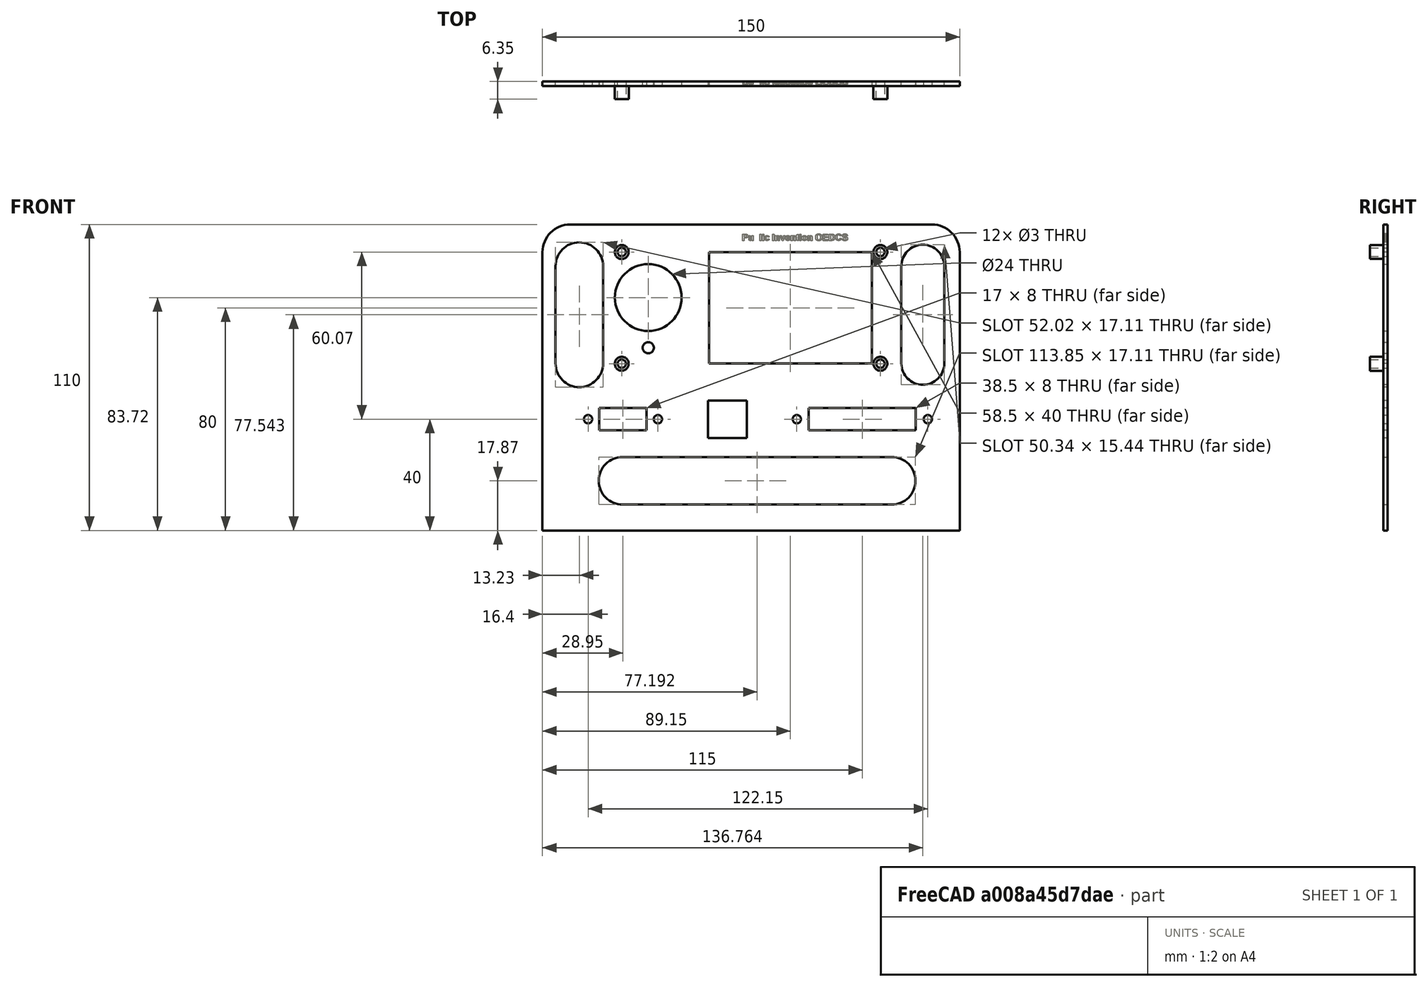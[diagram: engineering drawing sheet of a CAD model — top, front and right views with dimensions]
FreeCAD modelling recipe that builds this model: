
FCSTD DOCUMENT  (FreeCAD 0.19R24291 (Git))
Label: MountMini12864
License: All rights reserved
LicenseURL: http://en.wikipedia.org/wiki/All_rights_reserved
objects: TechDraw::DrawViewDimension×19, Sketcher::SketchObject×5, PartDesign::Pocket×4, PartDesign::Pad×2, Spreadsheet::Sheet×1, TechDraw::DrawSVGTemplate×1, PartDesign::Fillet×1, Part::Part2DObjectPython×1, PartDesign::Body×1, App::Part×1, TechDraw::DrawViewPart×1, TechDraw::DrawPage×1
note: 21 computed .brp shape members not serialized (recipe doc carries the construction recipe); baked Part::Feature solids carry a one-line shape summary decoded from their .brp

FEATURE [Sketcher::SketchObject] Sketch
  FullyConstrained = true
  MapMode = 5
  Placement = pos=(0,0,0) rot=(1,0,0;1.5708rad)
  Support = -> [XZ_Plane001]
  expr: Constraints[10] = <<Spreadsheet>>.Height
  expr: Constraints[9] = <<Spreadsheet>>.Width
  expr: Constraints[11] = <<Spreadsheet>>.OffsetVert
  expr: Constraints[12] = <<Spreadsheet>>.OffsetHorz
  sketch-geometry (5):
    g0: LineSegment StartX=-55 StartY=45 StartZ=0 EndX=95 EndY=45 EndZ=0
    g1: LineSegment StartX=95 StartY=45 StartZ=0 EndX=95 EndY=-65 EndZ=0
    g2: LineSegment StartX=95 StartY=-65 StartZ=0 EndX=-55 EndY=-65 EndZ=0
    g3: LineSegment StartX=-55 StartY=-65 StartZ=0 EndX=-55 EndY=45 EndZ=0
    g4: GeomPoint X=20 Y=-10 Z=0
  constraints (13):
    c: Coincident(g0,g1)
    c: Coincident(g1,g2)
    c: Coincident(g2,g3)
    c: Coincident(g3,g0)
    c: Horizontal(g0)
    c: Horizontal(g2)
    c: Vertical(g1)
    c: Vertical(g3)
    c: Symmetric(g0,g1,g4)
    c: DistanceX(g0,g0) = 150
    c: DistanceY(g3,g3) = 110
    c: DistanceY(g4,g-1) = 10
    c: DistanceX(g-1,g4) = 20
FEATURE [PartDesign::Pad] Pad  label="Pad Body"
  Direction = (1,1,1)
  Length = 1.5875
  Length2 = 100
  Placement = pos=(0,0,0) rot=(1,0,0;1.5708rad)
  Profile = -> Sketch
  Type = 0
  expr: Length = <<Spreadsheet>>.Thickness
FEATURE [Spreadsheet::Sheet] Spreadsheet
  cells = A1=MountMini12864; A2=Place a center point. Locate that point at Horz and Vertical Offset; A3=Place a rectangle around the point. ; A4=Select upper left corner, lower right cornder and center point. Set symetery; A5=Set Width to Width parameter (below), Set Height to Height Parameter below.; A6=Close the now fully parameterized and constrinaed sketch.; A7=Pad the sketch to the Depth prameter (below).; A9=Body; A10=OffsetHorz; B10(OffsetHorz)==20mm; A11=OffsetVert; B11(OffsetVert)==10mm; A13=Width; B13(Width)==150mm; C13=PCB is 189mm; A14=Height; B14(Height)==110mm; A15=Depth; B15(Depth)==3mm; A16=Thickness; B16(Thickness)==C16; C16==25.4 / 16; A18=DisplayMount; A19=OffsetMountHorz; B19(OffsetMountHorz)==20mm; C19=Toward left; A20=OffsetMountVert; B20(OffsetMountVert)==15mm; C21=From drawing; A22=DisplayMountWidth; B22(DisplayMountWidth)==C22; C22==101.99 - 8.99; A23=DisplayMountHeight; B23(DisplayMountHeight)==C23; C23==44 - 3.86; A24=DisplayMountHoleDiameter; B24(DisplayMountHoleDiameter)==3mm; A25=DisplayMountStandOffLength; B25(DisplayMountStandOffLength)==C25 * 25.4; C25=0.25; A27=OffsetDisplayHorz; B27(OffsetDisplayHorz)==61.6mm; C27=From edge; D27==70.59 - 8.99; A28=OffsetDisplayVert; B28(OffsetDisplayVert)==15mm; C28=From drawing; A29=DisplayWidth; B29(DisplayWidth)==58.5mm; C29==70.59 - 12.39; A30=DisplayHeight; B30(DisplayHeight)==40mm; C30==38.8mm; A32=OffsetEncoderHorz; B32(OffsetEncoderHorz)==12.53 - 3; C32=Guess; A33=OffserEncoderVert; B33(OffserEncoderVert)==(32.71 + 20.87) / 2 - 3; C33=Up from Mount; A34=EncoderDiameter; B34(EncoderDiameter)==24mm; C34=Measured Knob; A36=OffsetResetHorz; B36(OffsetResetHorz)==B32; C36=same as encoder; A37=OffserResetVert; B37(OffserResetVert)==5.75mm; C37=Up from Mount; A38=ResetDiameter; B38(ResetDiameter)==4mm; A41=DB25 Mount; A42=OffsetDB25MountHorz; B42(OffsetDB25MountHorz)==60mm; C42=This moves DB25, RJ12, and DB9; A43=OffsetDB25MountVert; B43(OffsetDB25MountVert)==25mm; C43=Down from center; A45=DB25MountWidth; B45(DB25MountWidth)==38.5mm; A46=DB25MountHeight; B46(DB25MountHeight)==8mm; A47=DB25MountHoleSpace; B47(DB25MountHoleSpace)==47.1mm; A48=DB25MountHoleDiameter; B48(DB25MountHoleDiameter)==3mm; A51=RJ12 Connector; A52=OffsetRJ12MountHorz; B52(OffsetRJ12MountHorz)==48.5mm; C52=From DB25; A53=OffsetRJ12MountVert; B53(OffsetRJ12MountVert)==25mm; A55=RJ12Width; B55(RJ12Width)==14mm; C55=13.5 mm measured; A56=RJ12Height; B56(RJ12Height)==13.5mm; C56=12.5 mm measured; A59=DB9 Mount; A60=OffsetDB9MountHorz; B60(OffsetDB9MountHorz)==86.05mm; A61=OffsetDB9MountVert; B61(OffsetDB9MountVert)==25mm; C61=Down from center; A63=DB9MountWidth; B63(DB9MountWidth)=17; C63==16.3mm; A64=DB9MountHeight; B64(DB9MountHeight)==8mm; A65=DB9MountHoleSpace; B65(DB9MountHoleSpace)==25.1mm; A66=DB9MountHoleDiameter; B66(DB9MountHoleDiameter)==3mm
FEATURE [Sketcher::SketchObject] Sketch001
  FullyConstrained = true
  MapMode = 5
  Placement = pos=(0,0,0) rot=(-1,0,0;1.5708rad)
  Support = -> [Pad]
  expr: Constraints[39] = <<Spreadsheet>>.OffsetMountHorz
  expr: Constraints[38] = <<Spreadsheet>>.OffsetEncoderHorz
  expr: Constraints[29] = <<Spreadsheet>>.DisplayWidth
  expr: Constraints[32] = <<Spreadsheet>>.OffsetDisplayHorz
  expr: Constraints[37] = <<Spreadsheet>>.OffserEncoderVert
  expr: Constraints[36] = <<Spreadsheet>>.OffserResetVert
  expr: Constraints[34] = <<Spreadsheet>>.ResetDiameter
  expr: Constraints[18] = <<Spreadsheet>>.DisplayMountHeight
  expr: Constraints[30] = <<Spreadsheet>>.DisplayHeight
  expr: Constraints[19] = <<Spreadsheet>>.OffsetMountVert
  expr: Constraints[33] = <<Spreadsheet>>.EncoderDiameter
  expr: Constraints[17] = <<Spreadsheet>>.DisplayMountWidth
  expr: Constraints[12] = <<Spreadsheet>>.DisplayMountHoleDiameter
  sketch-geometry (16):
    g0: LineSegment StartX=-26.5 StartY=5.07 StartZ=0 EndX=66.5 EndY=5.07 EndZ=0
    g1: LineSegment StartX=66.5 StartY=5.07 StartZ=0 EndX=66.5 EndY=-35.07 EndZ=0
    g2: LineSegment StartX=66.5 StartY=-35.07 StartZ=0 EndX=-26.5 EndY=-35.07 EndZ=0
    g3: LineSegment StartX=-26.5 StartY=-35.07 StartZ=0 EndX=-26.5 EndY=5.07 EndZ=0
    g4: GeomPoint X=20 Y=-15 Z=0
    g5: Circle CenterX=-26.5 CenterY=5.07 CenterZ=0 NormalX=0 NormalY=0 NormalZ=1 AngleXU=0 Radius=1.5
    g6: Circle CenterX=-26.5 CenterY=-35.07 CenterZ=0 NormalX=0 NormalY=0 NormalZ=1 AngleXU=0 Radius=1.5
    g7: Circle CenterX=66.5 CenterY=-35.07 CenterZ=0 NormalX=0 NormalY=0 NormalZ=1 AngleXU=0 Radius=1.5
    g8: Circle CenterX=66.5 CenterY=5.07 CenterZ=0 NormalX=0 NormalY=0 NormalZ=1 AngleXU=0 Radius=1.5
    g9: LineSegment StartX=4.9 StartY=5 StartZ=0 EndX=63.4 EndY=5 EndZ=0
    g10: LineSegment StartX=63.4 StartY=5 StartZ=0 EndX=63.4 EndY=-35 EndZ=0
    g11: LineSegment StartX=63.4 StartY=-35 StartZ=0 EndX=4.9 EndY=-35 EndZ=0
    g12: LineSegment StartX=4.9 StartY=-35 StartZ=0 EndX=4.9 EndY=5 EndZ=0
    g13: GeomPoint X=34.15 Y=-15 Z=0
    g14: Circle CenterX=-16.97 CenterY=-18.72 CenterZ=0 NormalX=0 NormalY=0 NormalZ=1 AngleXU=0 Radius=12
    g15: Circle CenterX=-16.97 CenterY=-0.68 CenterZ=0 NormalX=0 NormalY=0 NormalZ=1 AngleXU=0 Radius=2
  constraints (40):
    c: Coincident(g0,g1)
    c: Coincident(g1,g2)
    c: Coincident(g2,g3)
    c: Coincident(g3,g0)
    c: Horizontal(g0)
    c: Horizontal(g2)
    c: Vertical(g1)
    c: Vertical(g3)
    c: Symmetric(g0,g1,g4)
    c: Equal(g8,g7)
    c: Equal(g7,g6)
    c: Equal(g6,g5)
    c: Diameter(g5) = 3
    c: Coincident(g5,g0)
    c: Coincident(g6,g2)
    c: Coincident(g7,g1)
    c: Coincident(g8,g0)
    c: DistanceX(g0,g0) = 93
    c: DistanceY(g3,g3) = 40.14
    c: DistanceY(g4,g-1) = 15
    c: Coincident(g9,g10)
    c: Coincident(g10,g11)
    c: Coincident(g11,g12)
    c: Coincident(g12,g9)
    c: Horizontal(g9)
    c: Horizontal(g11)
    c: Vertical(g10)
    c: Vertical(g12)
    c: Symmetric(g9,g10,g13)
    c: DistanceX(g9,g9) = 58.5
    c: DistanceY(g10,g10) = 40
    c: Horizontal(g13,g4)
    c: DistanceX(g9,g8) = 61.6
    c: Diameter(g14) = 24
    c: Diameter(g15) = 4
    c: Vertical(g14,g15)
    c: DistanceY(g15,g5) = 5.75
    c: DistanceY(g14,g5) = 23.79
    c: DistanceX(g5,g14) = 9.53
    c: DistanceX(g-1,g4) = 20
FEATURE [PartDesign::Pocket] Pocket  label="PocketDisplayMountHoles"
  BaseFeature = -> Pad
  Length = 5
  Length2 = 100
  Placement = pos=(0,0,0) rot=(1,0,0;1.5708rad)
  Profile = -> Sketch001
  Type = 1
FEATURE [Sketcher::SketchObject] Sketch002
  FullyConstrained = true
  MapMode = 5
  Placement = pos=(0,0,0) rot=(-1,0,0;1.5708rad)
  Support = -> [Pocket]
  expr: Constraints[48] = <<Spreadsheet>>.DB9MountHoleSpace
  expr: Constraints[45] = <<Spreadsheet>>.OffsetDB9MountHorz
  expr: Constraints[42] = <<Spreadsheet>>.DB9MountWidth
  expr: Constraints[30] = <<Spreadsheet>>.RJ12Height
  expr: Constraints[32] = <<Spreadsheet>>.OffsetRJ12MountHorz
  expr: Constraints[29] = <<Spreadsheet>>.RJ12Width
  expr: Constraints[19] = <<Spreadsheet>>.OffsetDB25MountHorz
  expr: Constraints[43] = <<Spreadsheet>>.DB9MountHeight
  expr: Constraints[18] = <<Spreadsheet>>.DB25MountHoleSpace
  expr: Constraints[14] = <<Spreadsheet>>.DB25MountHoleDiameter
  expr: Constraints[9] = <<Spreadsheet>>.DB25MountWidth
  expr: Constraints[11] = <<Spreadsheet>>.OffsetDB25MountVert
  expr: Constraints[10] = <<Spreadsheet>>.DB25MountHeight
  sketch-geometry (21):
    g0: LineSegment StartX=40.75 StartY=29 StartZ=0 EndX=79.25 EndY=29 EndZ=0
    g1: LineSegment StartX=79.25 StartY=29 StartZ=0 EndX=79.25 EndY=21 EndZ=0
    g2: LineSegment StartX=79.25 StartY=21 StartZ=0 EndX=40.75 EndY=21 EndZ=0
    g3: LineSegment StartX=40.75 StartY=21 StartZ=0 EndX=40.75 EndY=29 EndZ=0
    g4: GeomPoint X=60 Y=25 Z=0
    g5: LineSegment StartX=36.45 StartY=25 StartZ=0 EndX=83.55 EndY=25 EndZ=0
    g6: Circle CenterX=36.45 CenterY=25 CenterZ=0 NormalX=0 NormalY=0 NormalZ=1 AngleXU=0 Radius=1.5
    g7: Circle CenterX=83.55 CenterY=25 CenterZ=0 NormalX=0 NormalY=0 NormalZ=1 AngleXU=0 Radius=1.5
    g8: LineSegment StartX=4.5 StartY=31.75 StartZ=0 EndX=18.5 EndY=31.75 EndZ=0
    g9: LineSegment StartX=18.5 StartY=31.75 StartZ=0 EndX=18.5 EndY=18.25 EndZ=0
    g10: LineSegment StartX=18.5 StartY=18.25 StartZ=0 EndX=4.5 EndY=18.25 EndZ=0
    g11: LineSegment StartX=4.5 StartY=18.25 StartZ=0 EndX=4.5 EndY=31.75 EndZ=0
    g12: GeomPoint X=11.5 Y=25 Z=0
    g13: LineSegment StartX=-34.55 StartY=29 StartZ=0 EndX=-17.55 EndY=29 EndZ=0
    g14: LineSegment StartX=-17.55 StartY=29 StartZ=0 EndX=-17.55 EndY=21 EndZ=0
    g15: LineSegment StartX=-17.55 StartY=21 StartZ=0 EndX=-34.55 EndY=21 EndZ=0
    g16: LineSegment StartX=-34.55 StartY=21 StartZ=0 EndX=-34.55 EndY=29 EndZ=0
    g17: GeomPoint X=-26.05 Y=25 Z=0
    g18: LineSegment StartX=-38.6 StartY=25 StartZ=0 EndX=-13.5 EndY=25 EndZ=0
    g19: Circle CenterX=-38.6 CenterY=25 CenterZ=0 NormalX=0 NormalY=0 NormalZ=1 AngleXU=0 Radius=1.5
    g20: Circle CenterX=-13.5 CenterY=25 CenterZ=0 NormalX=0 NormalY=0 NormalZ=1 AngleXU=0 Radius=1.5
  constraints (53):
    c: Coincident(g0,g1)
    c: Coincident(g1,g2)
    c: Coincident(g2,g3)
    c: Coincident(g3,g0)
    c: Horizontal(g0)
    c: Horizontal(g2)
    c: Vertical(g1)
    c: Vertical(g3)
    c: Symmetric(g0,g1,g4)
    c: DistanceX(g0,g0) = 38.5
    c: DistanceY(g3,g3) = 8
    c: DistanceY(g-1,g4) = 25
    c: Horizontal(g5)
    c: Symmetric(g5,g5,g4)
    c: Diameter(g6) = 3
    c: Equal(g6,g7)
    c: Coincident(g7,g5)
    c: Coincident(g6,g5)
    c: DistanceX(g5,g5) = 47.1
    c: DistanceX(g-1,g4) = 60
    c: Coincident(g8,g9)
    c: Coincident(g9,g10)
    c: Coincident(g10,g11)
    c: Coincident(g11,g8)
    c: Horizontal(g8)
    c: Horizontal(g10)
    c: Vertical(g9)
    c: Vertical(g11)
    c: Symmetric(g8,g9,g12)
    c: DistanceX(g8,g8) = 14
    c: DistanceY(g11,g11) = 13.5
    c: Horizontal(g12,g4)
    c: DistanceX(g12,g4) = 48.5
    c: Coincident(g13,g14)
    c: Coincident(g14,g15)
    c: Coincident(g15,g16)
    c: Coincident(g16,g13)
    c: Horizontal(g13)
    c: Horizontal(g15)
    c: Vertical(g14)
    c: Vertical(g16)
    c: Symmetric(g13,g14,g17)
    c: DistanceX(g13,g13) = 17
    c: DistanceY(g14,g14) = 8
    c: Horizontal(g17,g4)
    c: DistanceX(g17,g4) = 86.05
    c: Horizontal(g18)
    c: Symmetric(g18,g18,g17)
    c: DistanceX(g18,g18) = 25.1
    c: Equal(g19,g20)
    c: Equal(g20,g6)
    c: Coincident(g20,g18)
    c: Coincident(g19,g18)
FEATURE [PartDesign::Pocket] Pocket001  label="PockeDB25Mount"
  BaseFeature = -> Pocket
  Length = 5
  Length2 = 100
  Placement = pos=(0,0,0) rot=(1,0,0;1.5708rad)
  Profile = -> Sketch002
  Type = 1
FEATURE [TechDraw::DrawSVGTemplate] Template
  EditableTexts = Approved1=Approved 1; Approved2=Approved 2; CheckedBy=Checked By; Code=Code; CompanyAddress=1234 Main St; CompanyName=Company Name; DrawingNumber=Drawing Number; DrawingTitle1=Drawing Title 1; DrawingTitle2=Drawing Title 2; DrawingTitle3=Drawing Title 3; DrawnBy=Drawn By; Revision=Rev; Scale=Scale; Sheet=Sheet n of m
  Height = 215.9
  Orientation = 1
  Width = 279.4
FEATURE [Sketcher::SketchObject] Sketch003
  FullyConstrained = true
  MapMode = 5
  Placement = pos=(0,0,0) rot=(-1,0,0;1.5708rad)
  Support = -> [Pocket001]
  expr: Constraints[21] = <<Spreadsheet>>.DisplayMountHoleDiameter
  expr: Constraints[20] = <<Spreadsheet>>.OffsetDisplayVert
  expr: Constraints[19] = <<Spreadsheet>>.OffsetMountHorz
  expr: Constraints[18] = <<Spreadsheet>>.DisplayMountHeight
  expr: Constraints[17] = <<Spreadsheet>>.DisplayMountWidth
  sketch-geometry (13):
    g0: Circle CenterX=-26.5 CenterY=5.07 CenterZ=0 NormalX=0 NormalY=0 NormalZ=1 AngleXU=0 Radius=2.5
    g1: Circle CenterX=-26.5 CenterY=-35.07 CenterZ=0 NormalX=0 NormalY=0 NormalZ=1 AngleXU=0 Radius=2.5
    g2: Circle CenterX=66.5 CenterY=5.07 CenterZ=0 NormalX=0 NormalY=0 NormalZ=1 AngleXU=0 Radius=2.5
    g3: Circle CenterX=66.5 CenterY=-35.07 CenterZ=0 NormalX=0 NormalY=0 NormalZ=1 AngleXU=0 Radius=2.5
    g4: GeomPoint X=20 Y=-15 Z=0
    g5: LineSegment StartX=-26.5 StartY=5.07 StartZ=0 EndX=66.5 EndY=5.07 EndZ=0
    g6: LineSegment StartX=66.5 StartY=5.07 StartZ=0 EndX=66.5 EndY=-35.07 EndZ=0
    g7: LineSegment StartX=66.5 StartY=-35.07 StartZ=0 EndX=-26.5 EndY=-35.07 EndZ=0
    g8: LineSegment StartX=-26.5 StartY=-35.07 StartZ=0 EndX=-26.5 EndY=5.07 EndZ=0
    g9: Circle CenterX=-26.5 CenterY=5.07 CenterZ=0 NormalX=0 NormalY=0 NormalZ=1 AngleXU=0 Radius=1.5
    g10: Circle CenterX=-26.5 CenterY=-35.07 CenterZ=0 NormalX=0 NormalY=0 NormalZ=1 AngleXU=0 Radius=1.5
    g11: Circle CenterX=66.5 CenterY=5.07 CenterZ=0 NormalX=0 NormalY=0 NormalZ=1 AngleXU=0 Radius=1.5
    g12: Circle CenterX=66.5 CenterY=-35.07 CenterZ=0 NormalX=0 NormalY=0 NormalZ=1 AngleXU=0 Radius=1.5
  constraints (29):
    c: Diameter(g0) = 5
    c: Equal(g0,g2)
    c: Equal(g2,g1)
    c: Equal(g1,g3)
    c: Coincident(g5,g6)
    c: Coincident(g6,g7)
    c: Coincident(g7,g8)
    c: Coincident(g8,g5)
    c: Horizontal(g5)
    c: Horizontal(g7)
    c: Vertical(g6)
    c: Vertical(g8)
    c: Symmetric(g5,g6,g4)
    c: Coincident(g0,g5)
    c: Coincident(g1,g7)
    c: Coincident(g3,g6)
    c: Coincident(g2,g5)
    c: DistanceX(g5,g5) = 93
    c: DistanceY(g6,g6) = 40.14
    c: DistanceX(g-1,g4) = 20
    c: DistanceY(g4,g-1) = 15
    c: Diameter(g9) = 3
    c: Equal(g9,g10)
    c: Equal(g10,g12)
    c: Equal(g12,g11)
    c: Coincident(g9,g0)
    c: Coincident(g10,g1)
    c: Coincident(g3,g12)
    c: Coincident(g2,g11)
FEATURE [PartDesign::Pad] Pad001  label="Pad001MountStandoff"
  BaseFeature = -> Pocket001
  Direction = (1,1,1)
  Length = 6.35
  Length2 = 100
  Placement = pos=(0,0,0) rot=(1,0,0;1.5708rad)
  Profile = -> Sketch003
  Reversed = true
  Type = 0
  expr: Length = <<Spreadsheet>>.DisplayMountStandOffLength
FEATURE [Sketcher::SketchObject] Sketch004
  FullyConstrained = false
  MapMode = 5
  Placement = pos=(0,-1.5875,0) rot=(1,0,0;1.5708rad)
  Support = -> [Pad001]
  sketch-geometry (12):
    g0: ArcOfCircle CenterX=-26.1772 CenterY=-47.1305 CenterZ=0 NormalX=0 NormalY=0 NormalZ=1 AngleXU=0 Radius=8.555 StartAngle=1.5708 EndAngle=4.71239
    g1: ArcOfCircle CenterX=70.5609 CenterY=-47.1305 CenterZ=0 NormalX=0 NormalY=0 NormalZ=1 AngleXU=0 Radius=8.555 StartAngle=4.71239 EndAngle=7.85398
    g2: LineSegment StartX=-26.1772 StartY=-55.6855 StartZ=0 EndX=70.5609 EndY=-55.6855 EndZ=0
    g3: LineSegment StartX=-26.1772 StartY=-38.5755 StartZ=0 EndX=70.5609 EndY=-38.5755 EndZ=0
    g4: ArcOfCircle CenterX=-41.77 CenterY=29.9973 CenterZ=0 NormalX=0 NormalY=0 NormalZ=1 AngleXU=0 Radius=8.5548 StartAngle=1e-16 EndAngle=3.14159
    g5: ArcOfCircle CenterX=-41.77 CenterY=-4.91072 CenterZ=0 NormalX=0 NormalY=0 NormalZ=1 AngleXU=0 Radius=8.5548 StartAngle=3.14159 EndAngle=6.28319
    g6: LineSegment StartX=-50.3248 StartY=29.9973 StartZ=0 EndX=-50.3248 EndY=-4.91072 EndZ=0
    g7: LineSegment StartX=-33.2152 StartY=29.9973 StartZ=0 EndX=-33.2152 EndY=-4.91072 EndZ=0
    g8: ArcOfCircle CenterX=81.764 CenterY=29.9973 CenterZ=0 NormalX=0 NormalY=0 NormalZ=1 AngleXU=0 Radius=7.7185 StartAngle=2e-16 EndAngle=3.14159
    g9: ArcOfCircle CenterX=81.764 CenterY=-4.91072 CenterZ=0 NormalX=0 NormalY=0 NormalZ=1 AngleXU=0 Radius=7.7185 StartAngle=3.14159 EndAngle=6.28319
    g10: LineSegment StartX=74.0455 StartY=29.9973 StartZ=0 EndX=74.0455 EndY=-4.91072 EndZ=0
    g11: LineSegment StartX=89.4825 StartY=29.9973 StartZ=0 EndX=89.4825 EndY=-4.91072 EndZ=0
  constraints (25):
    c: Tangent(g0,g3) = 1.5708
    c: Tangent(g0,g2) = -1.5708
    c: Tangent(g2,g1) = -1.5708
    c: Tangent(g3,g1) = 1.5708
    c: Horizontal(g2)
    c: Equal(g0,g1)
    c: Tangent(g4,g7) = 1.5708
    c: Tangent(g4,g6) = -1.5708
    c: Tangent(g6,g5) = -1.5708
    c: Tangent(g7,g5) = 1.5708
    c: Vertical(g6)
    c: Equal(g4,g5)
    c: Tangent(g8,g11) = 1.5708
    c: Tangent(g8,g10) = -1.5708
    c: Tangent(g10,g9) = -1.5708
    c: Tangent(g11,g9) = 1.5708
    c: Vertical(g10)
    c: Equal(g8,g9)
    c: DistanceX(g4,g4) = 17.1096
    c: DistanceX(g8,g8) = 15.437
    c: Horizontal(g4,g8)
    c: Horizontal(g5,g9)
    c: DistanceX(g-1,g9) = 81.764
    c: DistanceX(g5,g9) = 123.534
    c: DistanceY(g0,g0) = 17.11
FEATURE [PartDesign::Pocket] Pocket002
  BaseFeature = -> Pad001
  Length = 5
  Length2 = 100
  Placement = pos=(0,0,0) rot=(1,0,0;1.5708rad)
  Profile = -> Sketch004
  Type = 1
FEATURE [PartDesign::Fillet] Fillet
  Base = -> Pocket002 [Edge2,Edge1]
  BaseFeature = -> Pocket002
  Placement = pos=(0,0,0) rot=(1,0,0;1.5708rad)
  Radius = 10
  SupportTransform = false
FEATURE [Part::Part2DObjectPython] ShapeString  # Draft 2D object (typed FeaturePython)
  FontFile = <path>
  Placement = pos=(16.7549,-4.66893e-06,39.1658) rot=(1,0,0;1.5708rad)
  Size = 2.54
  String = Public Invention OEDCS
  Tracking = 0
FEATURE [PartDesign::Pocket] Pocket003
  BaseFeature = -> Fillet
  Length = 1
  Length2 = 100
  Placement = pos=(0,0,0) rot=(1,0,0;1.5708rad)
  Profile = -> ShapeString
  Reversed = true
  Type = 0
FEATURE [PartDesign::Body] Body  label="Body_MountMini12864"
  Group = -> [Sketch,Pad,Sketch001,Pocket,Sketch002,Pocket001,Sketch003,Pad001,Sketch004,Pocket002,Fillet,ShapeString,Pocket003]
  Origin = -> Origin001
  Tip = -> Pocket003
FEATURE [App::Part] Part  label="Part_MountMini12864"
  Group = -> [Body]
  Origin = -> Origin
FEATURE [TechDraw::DrawViewPart] View
  CoarseView = false
  Direction = (0,1,0)
  Focus = 100
  HardHidden = false
  IsoCount = 0
  IsoHidden = false
  IsoVisible = false
  LockPosition = false
  Perspective = false
  Rotation = 0
  ScaleType = 2
  SeamHidden = false
  SeamVisible = true
  SmoothHidden = false
  SmoothVisible = true
  Source = -> [Part]
  X = 141.69
  XDirection = (-1,0,0)
  Y = 136.14
FEATURE [TechDraw::DrawViewDimension] Dimension
  Arbitrary = false
  ArbitraryTolerances = false
  EqualTolerance = true
  FormatSpec = %.3f
  FormatSpecOverTolerance = %+.3f
  FormatSpecUnderTolerance = %+.3f
  Inverted = false
  LockPosition = false
  MeasureType = 1
  OverTolerance = 0
  References2D = -> [View]
  Rotation = 0
  ScaleType = 2
  TheoreticalExact = false
  Type = 1
  UnderTolerance = 0
  X = -46.9351
  Y = 26.2363
FEATURE [TechDraw::DrawViewDimension] Dimension001
  Arbitrary = false
  ArbitraryTolerances = false
  EqualTolerance = true
  FormatSpec = %.3f
  FormatSpecOverTolerance = %+.3f
  FormatSpecUnderTolerance = %+.3f
  Inverted = false
  LockPosition = false
  MeasureType = 1
  OverTolerance = 0
  References2D = -> [View]
  Rotation = 0
  ScaleType = 2
  TheoreticalExact = false
  Type = 2
  UnderTolerance = 0
  X = -71.672
  Y = -29.179
FEATURE [TechDraw::DrawViewDimension] Dimension004
  Arbitrary = false
  ArbitraryTolerances = false
  EqualTolerance = true
  FormatSpec = ⌀%.3f
  FormatSpecOverTolerance = %+.3f
  FormatSpecUnderTolerance = %+.3f
  Inverted = false
  LockPosition = false
  MeasureType = 1
  OverTolerance = 0
  References2D = -> [View]
  Rotation = 0
  ScaleType = 2
  TheoreticalExact = false
  Type = 5
  UnderTolerance = 0
  X = 87.7226
  Y = 29.8842
FEATURE [TechDraw::DrawViewDimension] Dimension005
  Arbitrary = false
  ArbitraryTolerances = false
  EqualTolerance = true
  FormatSpec = ⌀%.3f
  FormatSpecOverTolerance = %+.3f
  FormatSpecUnderTolerance = %+.3f
  Inverted = false
  LockPosition = false
  MeasureType = 1
  OverTolerance = 0
  References2D = -> [View]
  Rotation = 0
  ScaleType = 2
  TheoreticalExact = false
  Type = 5
  UnderTolerance = 0
  X = 35.5581
  Y = -30.3195
FEATURE [TechDraw::DrawViewDimension] Dimension007
  Arbitrary = false
  ArbitraryTolerances = false
  EqualTolerance = true
  FormatSpec = %.3f
  FormatSpecOverTolerance = %+.3f
  FormatSpecUnderTolerance = %+.3f
  Inverted = false
  LockPosition = false
  MeasureType = 1
  OverTolerance = 0
  References2D = -> [View]
  Rotation = 0
  ScaleType = 2
  TheoreticalExact = false
  Type = 1
  UnderTolerance = 0
  X = -20.6064
  Y = 50.0465
FEATURE [TechDraw::DrawViewDimension] Dimension009
  Arbitrary = false
  ArbitraryTolerances = false
  EqualTolerance = true
  FormatSpec = %.3f
  FormatSpecOverTolerance = %+.3f
  FormatSpecUnderTolerance = %+.3f
  Inverted = false
  LockPosition = false
  MeasureType = 1
  OverTolerance = 0
  References2D = -> [View]
  Rotation = 0
  ScaleType = 2
  TheoreticalExact = false
  Type = 1
  UnderTolerance = 0
  X = 32.9041
  Y = 54.8532
FEATURE [TechDraw::DrawViewDimension] Dimension013
  Arbitrary = false
  ArbitraryTolerances = false
  EqualTolerance = true
  FormatSpec = %.3f
  FormatSpecOverTolerance = %+.3f
  FormatSpecUnderTolerance = %+.3f
  Inverted = false
  LockPosition = false
  MeasureType = 1
  OverTolerance = 0
  References2D = -> [View]
  Rotation = 0
  ScaleType = 2
  TheoreticalExact = false
  Type = 1
  UnderTolerance = 0
  X = 91.3994
  Y = -0.814891
FEATURE [TechDraw::DrawViewDimension] Dimension014
  Arbitrary = false
  ArbitraryTolerances = false
  EqualTolerance = true
  FormatSpec = %.3f
  FormatSpecOverTolerance = %+.3f
  FormatSpecUnderTolerance = %+.3f
  Inverted = false
  LockPosition = false
  MeasureType = 1
  OverTolerance = 0
  References2D = -> [View]
  Rotation = 0
  ScaleType = 2
  TheoreticalExact = false
  Type = 1
  UnderTolerance = 0
  X = 5.05625
  Y = -57.7938
FEATURE [TechDraw::DrawViewDimension] Dimension015
  Arbitrary = false
  ArbitraryTolerances = false
  EqualTolerance = true
  FormatSpec = %.3f
  FormatSpecOverTolerance = %+.3f
  FormatSpecUnderTolerance = %+.3f
  Inverted = false
  LockPosition = false
  MeasureType = 1
  OverTolerance = 0
  References2D = -> [View]
  Rotation = 0
  ScaleType = 2
  TheoreticalExact = false
  Type = 2
  UnderTolerance = 0
  X = -9.58058
  Y = -10.0272
FEATURE [TechDraw::DrawViewDimension] Dimension016
  Arbitrary = false
  ArbitraryTolerances = false
  EqualTolerance = true
  FormatSpec = %.3f
  FormatSpecOverTolerance = %+.3f
  FormatSpecUnderTolerance = %+.3f
  Inverted = false
  LockPosition = false
  MeasureType = 1
  OverTolerance = 0
  References2D = -> [View]
  Rotation = 0
  ScaleType = 2
  TheoreticalExact = false
  Type = 1
  UnderTolerance = 0
  X = -86.2432
  Y = -40.494
FEATURE [TechDraw::DrawViewDimension] Dimension017
  Arbitrary = false
  ArbitraryTolerances = false
  EqualTolerance = true
  FormatSpec = %.3f
  FormatSpecOverTolerance = %+.3f
  FormatSpecUnderTolerance = %+.3f
  Inverted = false
  LockPosition = false
  MeasureType = 1
  OverTolerance = 0
  References2D = -> [View]
  Rotation = 0
  ScaleType = 2
  TheoreticalExact = false
  Type = 1
  UnderTolerance = 0
  X = 99.8165
  Y = -7.76814
FEATURE [TechDraw::DrawViewDimension] Dimension018
  Arbitrary = false
  ArbitraryTolerances = false
  EqualTolerance = true
  FormatSpec = %.3f
  FormatSpecOverTolerance = %+.3f
  FormatSpecUnderTolerance = %+.3f
  Inverted = false
  LockPosition = false
  MeasureType = 1
  OverTolerance = 0
  References2D = -> [View]
  Rotation = 0
  ScaleType = 2
  TheoreticalExact = false
  Type = 1
  UnderTolerance = 0
  X = 82.2664
  Y = -55.464
FEATURE [TechDraw::DrawViewDimension] Dimension019
  Arbitrary = false
  ArbitraryTolerances = false
  EqualTolerance = true
  FormatSpec = %.3f
  FormatSpecOverTolerance = %+.3f
  FormatSpecUnderTolerance = %+.3f
  Inverted = false
  LockPosition = false
  MeasureType = 1
  OverTolerance = 0
  References2D = -> [View]
  Rotation = 0
  ScaleType = 2
  TheoreticalExact = false
  Type = 2
  UnderTolerance = 0
  X = 51.9089
  Y = -34.0732
FEATURE [TechDraw::DrawViewDimension] Dimension021
  Arbitrary = false
  ArbitraryTolerances = false
  EqualTolerance = true
  FormatSpec = %.3f
  FormatSpecOverTolerance = %+.3f
  FormatSpecUnderTolerance = %+.3f
  Inverted = false
  LockPosition = false
  MeasureType = 1
  OverTolerance = 0
  References2D = -> [View]
  Rotation = 0
  ScaleType = 2
  TheoreticalExact = false
  Type = 1
  UnderTolerance = 0
  X = -34.0152
  Y = 62.7763
FEATURE [TechDraw::DrawViewDimension] Dimension022
  Arbitrary = false
  ArbitraryTolerances = false
  EqualTolerance = true
  FormatSpec = %.3f
  FormatSpecOverTolerance = %+.3f
  FormatSpecUnderTolerance = %+.3f
  Inverted = false
  LockPosition = false
  MeasureType = 1
  OverTolerance = 0
  References2D = -> [View]
  Rotation = 0
  ScaleType = 2
  TheoreticalExact = false
  Type = 1
  UnderTolerance = 0
  X = -85.4324
  Y = 49.9656
FEATURE [TechDraw::DrawViewDimension] Dimension023
  Arbitrary = false
  ArbitraryTolerances = false
  EqualTolerance = true
  FormatSpec = %.3f
  FormatSpecOverTolerance = %+.3f
  FormatSpecUnderTolerance = %+.3f
  Inverted = false
  LockPosition = false
  MeasureType = 1
  OverTolerance = 0
  References2D = -> [View]
  Rotation = 0
  ScaleType = 2
  TheoreticalExact = false
  Type = 2
  UnderTolerance = 0
  X = 80.4755
  Y = -38.7945
FEATURE [TechDraw::DrawViewDimension] Dimension024
  Arbitrary = false
  ArbitraryTolerances = false
  EqualTolerance = true
  FormatSpec = %.3f
  FormatSpecOverTolerance = %+.3f
  FormatSpecUnderTolerance = %+.3f
  Inverted = false
  LockPosition = false
  MeasureType = 1
  OverTolerance = 0
  References2D = -> [View]
  Rotation = 0
  ScaleType = 2
  TheoreticalExact = false
  Type = 2
  UnderTolerance = 0
  X = -105.63
  Y = -25.5
FEATURE [TechDraw::DrawViewDimension] Dimension025
  Arbitrary = false
  ArbitraryTolerances = false
  EqualTolerance = true
  FormatSpec = %.3f
  FormatSpecOverTolerance = %+.3f
  FormatSpecUnderTolerance = %+.3f
  Inverted = false
  LockPosition = false
  MeasureType = 1
  OverTolerance = 0
  References2D = -> [View]
  Rotation = 0
  ScaleType = 2
  TheoreticalExact = false
  Type = 1
  UnderTolerance = 0
  X = -83.3792
  Y = 3.93382
FEATURE [TechDraw::DrawViewDimension] Dimension026
  Arbitrary = false
  ArbitraryTolerances = false
  EqualTolerance = true
  FormatSpec = %.3f
  FormatSpecOverTolerance = %+.3f
  FormatSpecUnderTolerance = %+.3f
  Inverted = false
  LockPosition = false
  MeasureType = 1
  OverTolerance = 0
  References2D = -> [View]
  Rotation = 0
  ScaleType = 2
  TheoreticalExact = false
  Type = 1
  UnderTolerance = 0
  X = -89.9939
  Y = -75.7733
FEATURE [TechDraw::DrawPage] Page
  KeepUpdated = true
  NextBalloonIndex = 1
  ProjectionType = 0
  Template = -> Template
  Views = -> [View,Dimension,Dimension001,Dimension004,Dimension005,Dimension007,Dimension009,Dimension013,Dimension014,Dimension015,Dimension016,Dimension017,Dimension018,Dimension019,Dimension021,Dimension022,Dimension023,Dimension024,Dimension025,Dimension026]
note: 1 file-system path scrubbed to <path> (originals preserved in the JSON sidecar)
